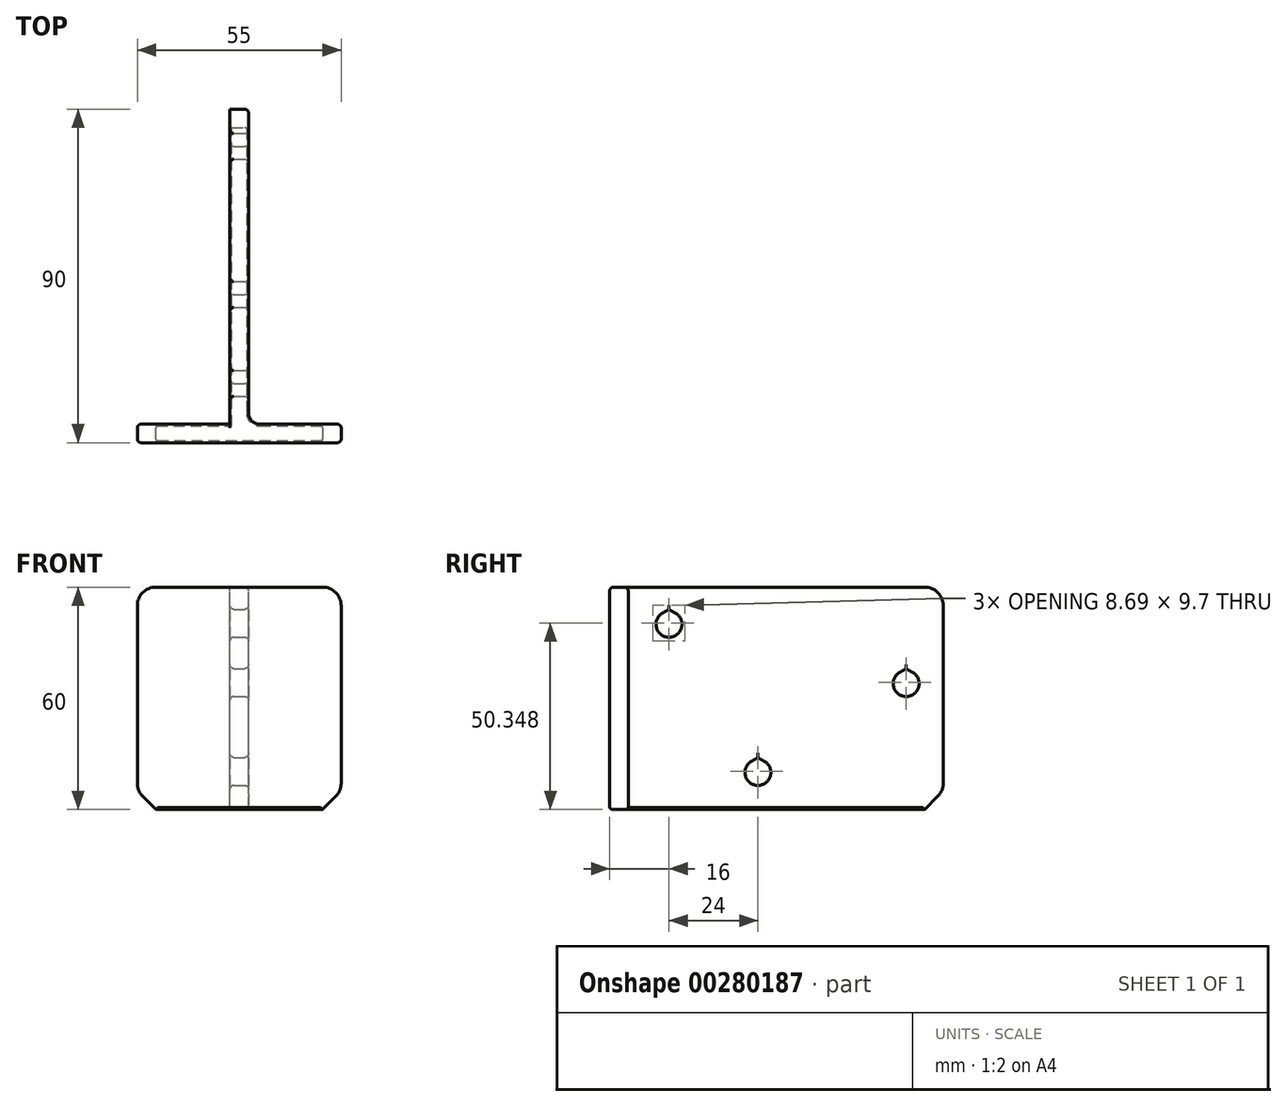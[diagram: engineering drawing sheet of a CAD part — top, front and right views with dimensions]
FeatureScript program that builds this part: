
annotation { "Feature Type Name" : "Feature", "Feature Type Description" : "" }
export const myFeature = defineFeature(function(context is Context, id is Id, definition is map)
    precondition{}
    {
        {
            var Q0;
            Q0=qCreatedBy(makeId("Right.planeOp"),FACE);
            var sketch = newSketch(context, id + "F0", { "sketchPlane" : qUnion([Q0])});
            skLineSegment(sketch, "E0.bottom", {"start": v(-35, 0) * mm, "end": v(50, 0) * mm});
            skLineSegment(sketch, "E0.top", {"start": v(-35, 60) * mm, "end": v(50, 60) * mm});
            skLineSegment(sketch, "E0.left", {"start": v(-35, 0) * mm, "end": v(-35, 60) * mm});
            skLineSegment(sketch, "E0.right", {"start": v(50, 0) * mm, "end": v(50, 60) * mm});
            skLineSegment(sketch, "E1", {"start": v(0, 10) * mm, "end": v(40, 34) * mm, "construction": true});
            skLineSegment(sketch, "E2", {"start": v(0, 10) * mm, "end": v(-24, 50) * mm, "construction": true});
            skSolve(sketch);
        }
        {
            var Q0;
            Q0 = qSketchRegion(id + "F0", true);
            extrude(context, id + "F1", {"entities" : qUnion([Q0]), "depth" : 5 * mm});
        }
        {
            var Q0;
            Q0=makeQuery(id+"F1.opExtrude","SWEPT_FACE",FACE,{"disambiguationData":[OSD([sQuery(id+"F0.wireOp",EDGE,"E0.left")])]});
            var sketch = newSketch(context, id + "F2", { "sketchPlane" : qUnion([Q0])});
            skLineSegment(sketch, "E3.bottom", {"start": v(-25, 0) * mm, "end": v(30, 0) * mm});
            skLineSegment(sketch, "E3.top", {"start": v(-25, 60) * mm, "end": v(30, 60) * mm});
            skLineSegment(sketch, "E3.left", {"start": v(-25, 0) * mm, "end": v(-25, 60) * mm});
            skLineSegment(sketch, "E3.right", {"start": v(30, 0) * mm, "end": v(30, 60) * mm});
            skSolve(sketch);
        }
        {
            var Q0;
            Q0 = qSketchRegion(id + "F2", true);
            extrude(context, id + "F3", {"entities" : qUnion([Q0]), "operationType" : NewBodyOperationType.ADD, "depth" : 5 * mm});
        }
        {
            var Q0;
            Q0=makeQuery(id+"F1.opExtrude","CAP_FACE",FACE,{"disambiguationData":[OSD([sQuery(id+"F0.wireOp",EDGE,"E0.bottom"),sQuery(id+"F0.wireOp",EDGE,"E0.top"),sQuery(id+"F0.wireOp",EDGE,"E0.left"),sQuery(id+"F0.wireOp",EDGE,"E0.right")])],"isStart":false});
            var sketch = newSketch(context, id + "F4", { "sketchPlane" : qUnion([Q0])});
            skLineSegment(sketch, "E4.0", {"start": v(0, 10) * mm, "end": v(-24, 50) * mm, "construction": true});
            skLineSegment(sketch, "E5.0", {"start": v(0, 10) * mm, "end": v(40, 34) * mm, "construction": true});
            skArc(sketch, "E6", {"start": v(-25.75, 53.03) * mm, "mid": v(-24, 46.5) * mm, "end": v(-22.25, 53.03) * mm});
            skLineSegment(sketch, "E7", {"start": v(-25.75, 53.03) * mm, "end": v(-24, 54.04) * mm});
            skLineSegment(sketch, "E8", {"start": v(-24, 54.04) * mm, "end": v(-22.25, 53.03) * mm});
            skArc(sketch, "E9", {"start": v(-1.75, 13.03) * mm, "mid": v(0, 6.5) * mm, "end": v(1.75, 13.03) * mm});
            skArc(sketch, "E10", {"start": v(38.25, 37.03) * mm, "mid": v(40, 30.5) * mm, "end": v(41.75, 37.03) * mm});
            skLineSegment(sketch, "E11", {"start": v(-1.75, 13.03) * mm, "end": v(0, 14.04) * mm});
            skLineSegment(sketch, "E12", {"start": v(0, 14.04) * mm, "end": v(1.75, 13.03) * mm});
            skLineSegment(sketch, "E13", {"start": v(38.25, 37.03) * mm, "end": v(40, 38.04) * mm});
            skLineSegment(sketch, "E14", {"start": v(40, 38.04) * mm, "end": v(41.75, 37.03) * mm});
            skSolve(sketch);
        }
        {
            var Q0;
            Q0 = qSketchRegion(id + "F4", true);
            extrude(context, id + "F5", {"entities" : qUnion([Q0]), "operationType" : NewBodyOperationType.REMOVE, "endBound" : BoundingType.UP_TO_NEXT, "oppositeDirection" : true, "depth" : 25 * mm});
        }
        {
            var Q0;
            Q0=makeQuery(id+"F1.opExtrude","CAP_EDGE",EDGE,{"disambiguationData":[OSD([sQuery(id+"F0.wireOp",EDGE,"E0.left")])],"isStart":false});
            var Q1;
            Q1=makeQuery(id+"F1.opExtrude","CAP_EDGE",EDGE,{"disambiguationData":[OSD([sQuery(id+"F0.wireOp",EDGE,"E0.left")])],"isStart":true});
            fillet(context, id + "F6", {"entities" : qUnion([Q0, Q1]), "radius" : 3 * mm, "tangentPropagation" : true, "allowEdgeOverflow" : false});
        }
        {
            var Q0;
            Q0=makeQuery(id+"F3.opExtrude","SWEPT_EDGE",EDGE,{"disambiguationData":[OSD([sQuery(id+"F2.wireOp",EDGE,"E3.bottom"),sQuery(id+"F2.wireOp",EDGE,"E3.right")])]});
            var Q1;
            Q1=makeQuery(id+"F1.opExtrude","SWEPT_EDGE",EDGE,{"disambiguationData":[OSD([sQuery(id+"F0.wireOp",EDGE,"E0.bottom"),sQuery(id+"F0.wireOp",EDGE,"E0.right")])]});
            var Q2;
            Q2=makeQuery(id+"F3.opExtrude","SWEPT_EDGE",EDGE,{"disambiguationData":[OSD([sQuery(id+"F2.wireOp",EDGE,"E3.bottom"),sQuery(id+"F2.wireOp",EDGE,"E3.left")])]});
            chamfer(context, id + "F7", {"entities" : qUnion([Q0, Q1, Q2]), "width" : 5 * mm, "tangentPropagation" : true});
        }
        {
            var Q0;
            Q0=makeQuery(id+"F3.opExtrude","SWEPT_EDGE",EDGE,{"disambiguationData":[OSD([sQuery(id+"F2.wireOp",EDGE,"E3.top"),sQuery(id+"F2.wireOp",EDGE,"E3.right")])]});
            var Q1;
            Q1=makeQuery(id+"F3.opExtrude","SWEPT_EDGE",EDGE,{"disambiguationData":[OSD([sQuery(id+"F2.wireOp",EDGE,"E3.top"),sQuery(id+"F2.wireOp",EDGE,"E3.left")])]});
            var Q2;
            Q2=makeQuery(id+"F1.opExtrude","SWEPT_EDGE",EDGE,{"disambiguationData":[OSD([sQuery(id+"F0.wireOp",EDGE,"E0.top"),sQuery(id+"F0.wireOp",EDGE,"E0.right")])]});
            var Q3;
            {var subQ0=sQuery(id+"F2.wireOp",EDGE,"E3.right");Q3=makeQuery(id+"F7.opChamfer","BLEND_EDGE",EDGE,{"blendedFrom":[makeQuery(id+"F3.opExtrude","SWEPT_EDGE",EDGE,{"disambiguationData":[OSD([sQuery(id+"F2.wireOp",EDGE,"E3.bottom"),subQ0])]}),makeQuery(id+"F3.opExtrude","SWEPT_FACE",FACE,{"disambiguationData":[OSD([subQ0])]})],"blendedInto":[makeQuery(id+"F3.opExtrude","SWEPT_FACE",FACE,{"disambiguationData":[OSD([subQ0])]})]});}
            var Q4;
            {var subQ0=sQuery(id+"F0.wireOp",EDGE,"E0.right");Q4=makeQuery(id+"F7.opChamfer","BLEND_EDGE",EDGE,{"blendedFrom":[makeQuery(id+"F1.opExtrude","SWEPT_EDGE",EDGE,{"disambiguationData":[OSD([sQuery(id+"F0.wireOp",EDGE,"E0.bottom"),subQ0])]}),makeQuery(id+"F1.opExtrude","SWEPT_FACE",FACE,{"disambiguationData":[OSD([subQ0])]})],"blendedInto":[makeQuery(id+"F1.opExtrude","SWEPT_FACE",FACE,{"disambiguationData":[OSD([subQ0])]})]});}
            var Q5;
            {var subQ0=sQuery(id+"F2.wireOp",EDGE,"E3.left");Q5=makeQuery(id+"F7.opChamfer","BLEND_EDGE",EDGE,{"blendedFrom":[makeQuery(id+"F3.opExtrude","SWEPT_EDGE",EDGE,{"disambiguationData":[OSD([sQuery(id+"F2.wireOp",EDGE,"E3.bottom"),subQ0])]}),makeQuery(id+"F3.opExtrude","SWEPT_FACE",FACE,{"disambiguationData":[OSD([subQ0])]})],"blendedInto":[makeQuery(id+"F3.opExtrude","SWEPT_FACE",FACE,{"disambiguationData":[OSD([subQ0])]})]});}
            fillet(context, id + "F8", {"entities" : qUnion([Q0, Q1, Q2, Q3, Q4, Q5]), "radius" : 5 * mm, "tangentPropagation" : true, "allowEdgeOverflow" : false});
        }
        {
            var Q0;
            Q0=makeQuery(id+"F3.opExtrude","CAP_EDGE",EDGE,{"disambiguationData":[OSD([sQuery(id+"F2.wireOp",EDGE,"E3.right")])],"isStart":true});
            var Q1;
            Q1=makeQuery(id+"F3.opExtrude","CAP_EDGE",EDGE,{"disambiguationData":[OSD([sQuery(id+"F2.wireOp",EDGE,"E3.left")])],"isStart":true});
            var Q2;
            Q2=makeQuery(id+"F3.opExtrude","CAP_EDGE",EDGE,{"disambiguationData":[OSD([sQuery(id+"F2.wireOp",EDGE,"E3.right")])],"isStart":false});
            var Q3;
            Q3=makeQuery(id+"F5.boolean.opBoolean","COPY",FACE,{"derivedFrom":makeQuery(id+"F5.opExtrude","SWEPT_FACE",FACE,{"disambiguationData":[OSD([sQuery(id+"F4.wireOp",EDGE,"E6")])]})});
            var Q4;
            Q4=makeQuery(id+"F5.boolean.opBoolean","COPY",FACE,{"derivedFrom":makeQuery(id+"F5.opExtrude","SWEPT_FACE",FACE,{"disambiguationData":[OSD([sQuery(id+"F4.wireOp",EDGE,"E9")])]})});
            var Q5;
            Q5=makeQuery(id+"F5.boolean.opBoolean","COPY",FACE,{"derivedFrom":makeQuery(id+"F5.opExtrude","SWEPT_FACE",FACE,{"disambiguationData":[OSD([sQuery(id+"F4.wireOp",EDGE,"E10")])]})});
            fillet(context, id + "F9", {"entities" : qUnion([Q0, Q1, Q2, Q3, Q4, Q5]), "radius" : 1 * mm, "tangentPropagation" : true, "allowEdgeOverflow" : false});
        }
        {
            var Q0;
            {var subQ0=sQuery(id+"F2.wireOp",EDGE,"E3.left");var subQ1=sQuery(id+"F2.wireOp",EDGE,"E3.bottom");Q0=makeQuery(id+"F3.boolean.opBoolean","SPLIT",EDGE,{"disambiguationData":[TD([makeQuery(id+"F3.opExtrude","SWEPT_FACE",FACE,{"disambiguationData":[OSD([subQ0])]})])],"derivedFrom":makeQuery(id+"F3.opExtrude","CAP_EDGE",EDGE,{"disambiguationData":[OSD([subQ1])],"isStart":true})});}
            var Q1;
            Q1=makeQuery(id+"F6.opFillet","BLEND_EDGE",EDGE,{"blendedFrom":[makeQuery(id+"F1.opExtrude","CAP_EDGE",EDGE,{"disambiguationData":[OSD([sQuery(id+"F0.wireOp",EDGE,"E0.left")])],"isStart":true}),makeQuery(id+"F3.boolean.opBoolean","MERGE",FACE,{"derivedFrom":[makeQuery(id+"F1.opExtrude","SWEPT_FACE",FACE,{"disambiguationData":[OSD([sQuery(id+"F0.wireOp",EDGE,"E0.bottom")])]}),makeQuery(id+"F3.opExtrude","SWEPT_FACE",FACE,{"disambiguationData":[OSD([sQuery(id+"F2.wireOp",EDGE,"E3.bottom")])]})]})],"blendedInto":[makeQuery(id+"F3.boolean.opBoolean","MERGE",FACE,{"derivedFrom":[makeQuery(id+"F1.opExtrude","SWEPT_FACE",FACE,{"disambiguationData":[OSD([sQuery(id+"F0.wireOp",EDGE,"E0.bottom")])]}),makeQuery(id+"F3.opExtrude","SWEPT_FACE",FACE,{"disambiguationData":[OSD([sQuery(id+"F2.wireOp",EDGE,"E3.bottom")])]})]})]});
            var Q2;
            Q2=makeQuery(id+"F1.opExtrude","CAP_EDGE",EDGE,{"disambiguationData":[OSD([sQuery(id+"F0.wireOp",EDGE,"E0.bottom")])],"isStart":true});
            var Q3;
            Q3=makeQuery(id+"F1.opExtrude","CAP_EDGE",EDGE,{"disambiguationData":[OSD([sQuery(id+"F0.wireOp",EDGE,"E0.bottom")])],"isStart":false});
            var Q4;
            Q4=makeQuery(id+"F6.opFillet","BLEND_EDGE",EDGE,{"blendedFrom":[makeQuery(id+"F1.opExtrude","CAP_EDGE",EDGE,{"disambiguationData":[OSD([sQuery(id+"F0.wireOp",EDGE,"E0.left")])],"isStart":false}),makeQuery(id+"F3.boolean.opBoolean","MERGE",FACE,{"derivedFrom":[makeQuery(id+"F1.opExtrude","SWEPT_FACE",FACE,{"disambiguationData":[OSD([sQuery(id+"F0.wireOp",EDGE,"E0.bottom")])]}),makeQuery(id+"F3.opExtrude","SWEPT_FACE",FACE,{"disambiguationData":[OSD([sQuery(id+"F2.wireOp",EDGE,"E3.bottom")])]})]})],"blendedInto":[makeQuery(id+"F3.boolean.opBoolean","MERGE",FACE,{"derivedFrom":[makeQuery(id+"F1.opExtrude","SWEPT_FACE",FACE,{"disambiguationData":[OSD([sQuery(id+"F0.wireOp",EDGE,"E0.bottom")])]}),makeQuery(id+"F3.opExtrude","SWEPT_FACE",FACE,{"disambiguationData":[OSD([sQuery(id+"F2.wireOp",EDGE,"E3.bottom")])]})]})]});
            var Q5;
            {var subQ1=sQuery(id+"F2.wireOp",EDGE,"E3.right");var subQ2=sQuery(id+"F2.wireOp",EDGE,"E3.bottom");Q5=makeQuery(id+"F3.boolean.opBoolean","SPLIT",EDGE,{"disambiguationData":[TD([makeQuery(id+"F3.opExtrude","SWEPT_FACE",FACE,{"disambiguationData":[OSD([subQ1])]})])],"derivedFrom":makeQuery(id+"F3.opExtrude","CAP_EDGE",EDGE,{"disambiguationData":[OSD([subQ2])],"isStart":true})});}
            var Q6;
            Q6=makeQuery(id+"F3.opExtrude","CAP_EDGE",EDGE,{"disambiguationData":[OSD([sQuery(id+"F2.wireOp",EDGE,"E3.bottom")])],"isStart":false});
            chamfer(context, id + "F10", {"entities" : qUnion([Q0, Q1, Q2, Q3, Q4, Q5, Q6]), "width" : .5 * mm});
        }
    });
